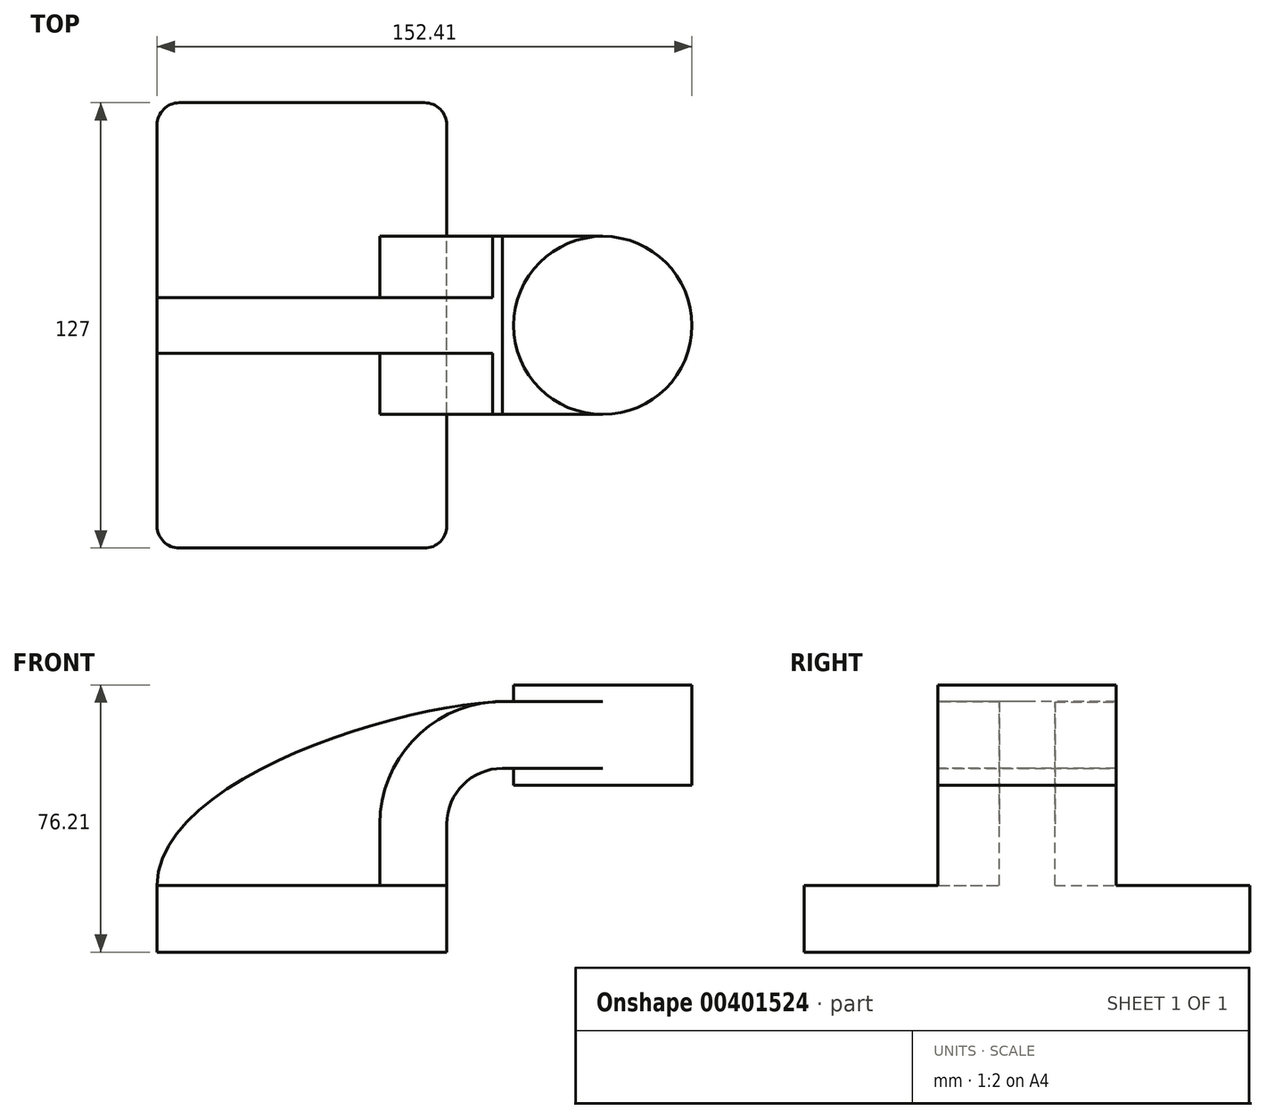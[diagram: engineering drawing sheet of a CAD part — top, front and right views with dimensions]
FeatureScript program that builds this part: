
annotation { "Feature Type Name" : "Feature", "Feature Type Description" : "" }
export const myFeature = defineFeature(function(context is Context, id is Id, definition is map)
    precondition{}
    {
        {
            var Q0;
            Q0=qCreatedBy(makeId("Front.planeOp"),FACE);
            var sketch = newSketch(context, id + "F0", { "sketchPlane" : qUnion([Q0])});
            skLineSegment(sketch, "E0.bottom", {"start": v(-41.28, -9.53) * mm, "end": v(41.28, -9.53) * mm});
            skLineSegment(sketch, "E0.top", {"start": v(-41.28, 9.52) * mm, "end": v(41.28, 9.52) * mm});
            skLineSegment(sketch, "E0.left", {"start": v(-41.28, -9.53) * mm, "end": v(-41.28, 9.52) * mm});
            skLineSegment(sketch, "E0.right", {"start": v(41.28, -9.53) * mm, "end": v(41.28, 9.52) * mm});
            skPoint(sketch, "E0.middle", {"position": v(0, 0) * mm});
            skLineSegment(sketch, "E1.bottom", {"start": v(60.32, 66.67) * mm, "end": v(111.12, 66.67) * mm});
            skLineSegment(sketch, "E1.top", {"start": v(60.32, 38.1) * mm, "end": v(111.12, 38.1) * mm});
            skLineSegment(sketch, "E1.left", {"start": v(60.32, 66.67) * mm, "end": v(60.32, 38.1) * mm});
            skLineSegment(sketch, "E1.right", {"start": v(111.12, 66.67) * mm, "end": v(111.12, 38.1) * mm});
            skPoint(sketch, "E1.middle", {"position": v(85.72, 52.39) * mm});
            skLineSegment(sketch, "E2", {"start": v(41.27, 9.52) * mm, "end": v(41.27, 27) * mm});
            skArc(sketch, "E3", {"start": v(41.27, 27) * mm, "mid": v(45.92, 38.23) * mm, "end": v(57.15, 42.88) * mm});
            skLineSegment(sketch, "E4", {"start": v(57.15, 42.88) * mm, "end": v(85.72, 42.88) * mm});
            skLineSegment(sketch, "E5.0", {"start": v(57.15, 61.93) * mm, "end": v(85.72, 61.93) * mm});
            skArc(sketch, "E5.1", {"start": v(22.22, 27) * mm, "mid": v(32.45, 51.7) * mm, "end": v(57.15, 61.93) * mm});
            skLineSegment(sketch, "E5.2", {"start": v(22.22, 9.52) * mm, "end": v(22.22, 27) * mm});
            skLineSegment(sketch, "E6", {"start": v(85.72, 38.1) * mm, "end": v(85.72, 66.67) * mm});
            skFitSpline(sketch, "E7", {"points": [v(-41.28, 9.52) * mm, v(57.15, 61.93) * mm], "startDerivative": vector(0.92, 92.98) * mm, "endDerivative": vector(82.42, 1.53) * mm});
            skSolve(sketch);
        }
        {
            var Q0;
            Q0=makeQuery(id+"F0.imprint","IMPRINT",FACE,{"disambiguationData":[TD([[makeQuery(id+"F0.imprint","IMPRINT",EDGE,{"derivedFrom":sQuery(id+"F0.wireOp",EDGE,"E0.bottom")}),1.0]])]});
            extrude(context, id + "F1", {"entities" : qUnion([Q0]), "endBound" : BoundingType.SYMMETRIC, "depth" : 127 * mm});
        }
        {
            var Q0;
            {var subQ1=sQuery(id+"F0.wireOp",EDGE,"E2");Q0=makeQuery(id+"F0.imprint","IMPRINT",FACE,{"disambiguationData":[TD([[makeQuery(id+"F0.imprint","IMPRINT",EDGE,{"derivedFrom":subQ1}),1.0]])]});}
            var Q1;
            {var subQ0=sQuery(id+"F0.wireOp",EDGE,"E5.0");var subQ1=sQuery(id+"F0.wireOp",EDGE,"E1.left");var subQ2=makeQuery(id+"F0.imprint","INTERSECT",VERTEX,{"derivedFrom":[subQ1,subQ0]});Q1=makeQuery(id+"F0.imprint","IMPRINT",FACE,{"disambiguationData":[TD([[makeQuery(id+"F0.imprint","IMPRINT",EDGE,{"disambiguationData":[TD([[subQ2,-1.0]])],"derivedFrom":subQ1}),1.0]])]});}
            extrude(context, id + "F2", {"entities" : qUnion([Q0, Q1]), "operationType" : NewBodyOperationType.ADD, "endBound" : BoundingType.SYMMETRIC, "depth" : 50.8 * mm});
        }
        {
            var Q0;
            {var subQ3=sQuery(id+"F0.wireOp",EDGE,"E5.2");Q0=makeQuery(id+"F0.imprint","IMPRINT",FACE,{"disambiguationData":[TD([[makeQuery(id+"F0.imprint","IMPRINT",EDGE,{"derivedFrom":subQ3}),1.0]])]});}
            extrude(context, id + "F3", {"entities" : qUnion([Q0]), "operationType" : NewBodyOperationType.ADD, "endBound" : BoundingType.SYMMETRIC, "depth" : 15.88 * mm});
        }
        {
            var Q0;
            {var subQ4=sQuery(id+"F0.wireOp",EDGE,"E1.right");Q0=makeQuery(id+"F0.imprint","IMPRINT",FACE,{"disambiguationData":[TD([[makeQuery(id+"F0.imprint","IMPRINT",EDGE,{"derivedFrom":subQ4}),-1.0]])]});}
            var Q1;
            Q1=sQuery(id+"F0.wireOp",EDGE,"E6");
            revolve(context, id + "F4", {"operationType" : NewBodyOperationType.ADD, "entities" : qUnion([Q0]), "axis" : qUnion([Q1]), "revolveType" : RevolveType.FULL});
        }
        {
            var Q0;
            Q0=makeQuery(id+"F1.opExtrude","CAP_EDGE",EDGE,{"disambiguationData":[OSD([sQuery(id+"F0.wireOp",EDGE,"E0.left")])],"isStart":true});
            var Q1;
            Q1=makeQuery(id+"F1.opExtrude","CAP_EDGE",EDGE,{"disambiguationData":[OSD([sQuery(id+"F0.wireOp",EDGE,"E0.left")])],"isStart":false});
            var Q2;
            Q2=makeQuery(id+"F1.opExtrude","CAP_EDGE",EDGE,{"disambiguationData":[OSD([sQuery(id+"F0.wireOp",EDGE,"E0.right")])],"isStart":true});
            var Q3;
            Q3=makeQuery(id+"F1.opExtrude","CAP_EDGE",EDGE,{"disambiguationData":[OSD([sQuery(id+"F0.wireOp",EDGE,"E0.right")])],"isStart":false});
            fillet(context, id + "F5", {"entities" : qUnion([Q0, Q1, Q2, Q3]), "radius" : 6.35 * mm, "tangentPropagation" : true, "allowEdgeOverflow" : false});
        }
    });
